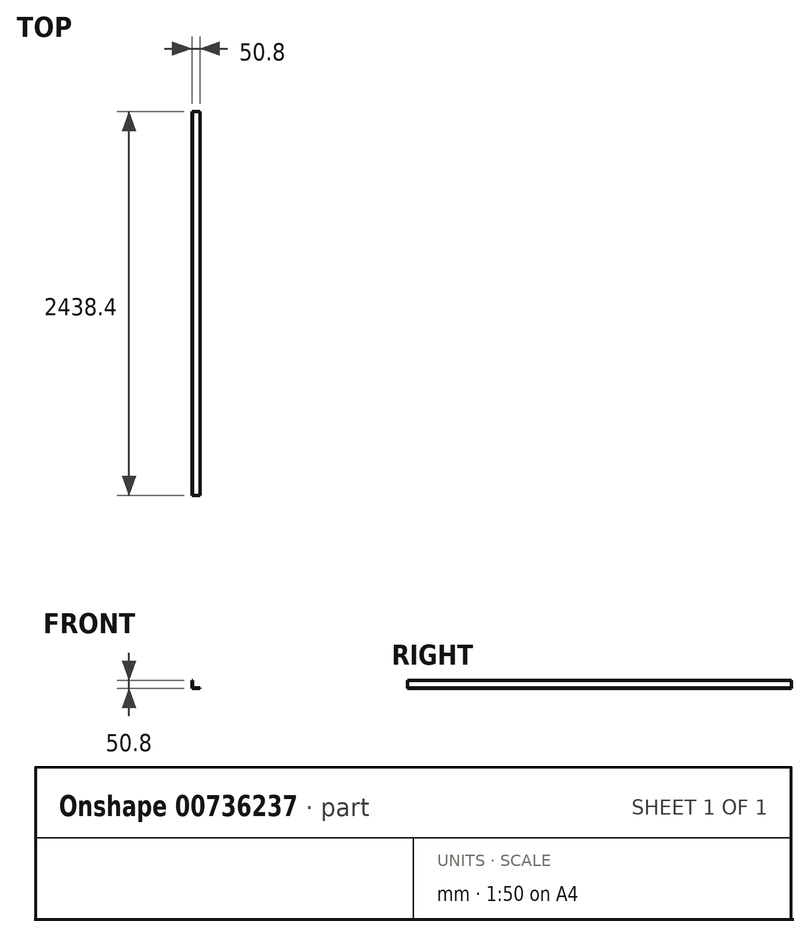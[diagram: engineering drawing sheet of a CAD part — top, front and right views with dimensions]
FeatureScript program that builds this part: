
annotation { "Feature Type Name" : "Feature", "Feature Type Description" : "" }
export const myFeature = defineFeature(function(context is Context, id is Id, definition is map)
    precondition{}
    {
        {
            var Q0;
            Q0=qCreatedBy(makeId("Front.planeOp"),FACE);
            var sketch = newSketch(context, id + "F0", { "sketchPlane" : qUnion([Q0])});
            skLineSegment(sketch, "E0.bottom", {"start": v(0, 0) * mm, "end": v(50.8, 0) * mm});
            skLineSegment(sketch, "E0.top", {"start": v(0, 3.18) * mm, "end": v(50.8, 3.18) * mm});
            skLineSegment(sketch, "E0.left", {"start": v(0, 0) * mm, "end": v(0, 3.18) * mm});
            skLineSegment(sketch, "E0.right", {"start": v(50.8, 0) * mm, "end": v(50.8, 3.18) * mm});
            skLineSegment(sketch, "E1.bottom", {"start": v(0, 0) * mm, "end": v(3.18, 0) * mm});
            skLineSegment(sketch, "E1.top", {"start": v(0, 50.8) * mm, "end": v(3.17, 50.8) * mm});
            skLineSegment(sketch, "E1.left", {"start": v(0, 0) * mm, "end": v(0, 50.8) * mm});
            skLineSegment(sketch, "E1.right", {"start": v(3.18, 0) * mm, "end": v(3.17, 50.8) * mm});
            skSolve(sketch);
        }
        {
            var Q0;
            Q0=qSketchRegion(id+"F0",true);
            extrude(context, id + "F1", {"entities" : qUnion([Q0]), "oppositeDirection" : true, "depth" : 2438.4 * mm, "offsetDistance" : 25.4 * mm});
        }
    });
